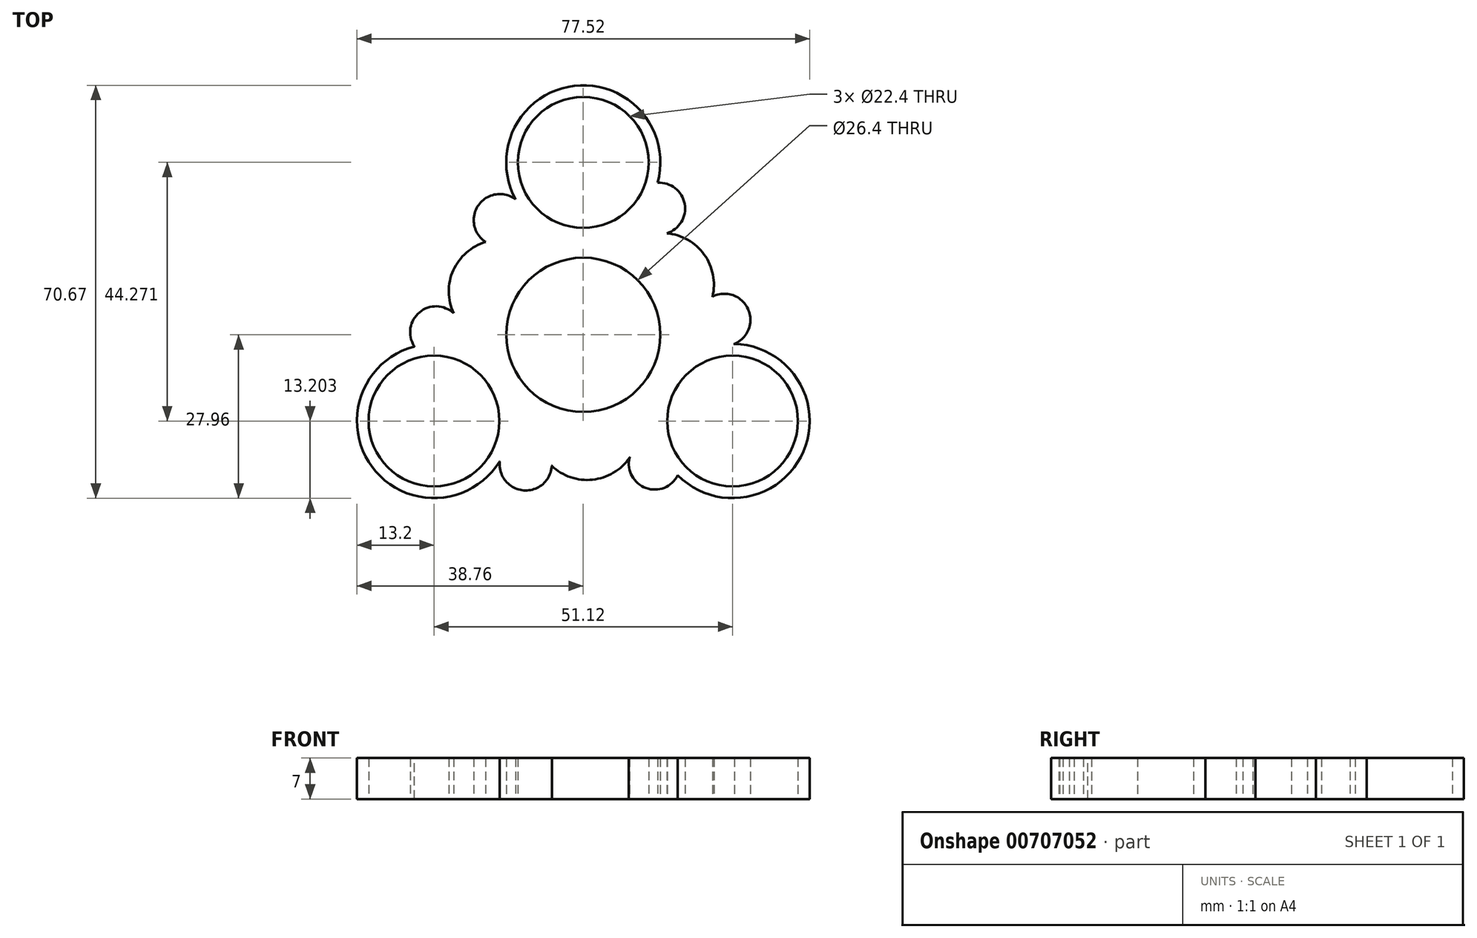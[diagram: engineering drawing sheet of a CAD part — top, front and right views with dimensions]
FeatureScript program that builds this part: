
annotation { "Feature Type Name" : "Feature", "Feature Type Description" : "" }
export const myFeature = defineFeature(function(context is Context, id is Id, definition is map)
    precondition{}
    {
        {
            var Q0;
            Q0=qCreatedBy(makeId("Top.planeOp"),FACE);
            var sketch = newSketch(context, id + "F0", { "sketchPlane" : qUnion([Q0])});
            skCircle(sketch, "E0", {"center": v(0, 0) * mm, "radius": 11.2 * mm});
            skCircle(sketch, "E1", {"center": v(0, 0) * mm, "radius": 13.2 * mm});
            skCircle(sketch, "E2", {"center": v(0, 29.51) * mm, "radius": 11.2 * mm});
            skCircle(sketch, "E3", {"center": v(0, 29.51) * mm, "radius": 13.2 * mm});
            skCircle(sketch, "E4.1.0", {"center": v(-25.56, -14.76) * mm, "radius": 11.2 * mm});
            skCircle(sketch, "E4.1.1", {"center": v(-25.56, -14.76) * mm, "radius": 13.2 * mm});
            skCircle(sketch, "E4.2.0", {"center": v(25.56, -14.76) * mm, "radius": 11.2 * mm});
            skCircle(sketch, "E4.2.1", {"center": v(25.56, -14.76) * mm, "radius": 13.2 * mm});
            skArc(sketch, "E5", {"start": v(-22.2, -2) * mm, "mid": v(-12.24, 8.63) * mm, "end": v(-11.58, 23.18) * mm});
            skArc(sketch, "E6.1.0", {"start": v(12.83, -18.23) * mm, "mid": v(-1.35, -14.91) * mm, "end": v(-14.28, -21.61) * mm});
            skArc(sketch, "E6.2.0", {"start": v(9.38, 20.22) * mm, "mid": v(13.6, 6.28) * mm, "end": v(25.86, -1.56) * mm});
            skArc(sketch, "E7", {"start": v(-10.62, 15.51) * mm, "mid": v(-21.97, 11.62) * mm, "end": v(-18.98, 0) * mm});
            skArc(sketch, "E8.1.0", {"start": v(-8.12, -16.96) * mm, "mid": v(0.93, -24.84) * mm, "end": v(9.49, -16.44) * mm});
            skArc(sketch, "E8.2.0", {"start": v(18.75, 1.45) * mm, "mid": v(21.05, 13.22) * mm, "end": v(9.49, 16.44) * mm});
            skArc(sketch, "E9", {"start": v(-11.58, 23.18) * mm, "mid": v(-17.93, 22.2) * mm, "end": v(-16.74, 15.9) * mm});
            skArc(sketch, "E10", {"start": v(-22.2, 3.69) * mm, "mid": v(-28.08, 3.83) * mm, "end": v(-28.92, -2) * mm});
            skArc(sketch, "E11.1.0", {"start": v(-14.28, -21.61) * mm, "mid": v(-10.27, -26.63) * mm, "end": v(-5.4, -22.44) * mm});
            skArc(sketch, "E11.1.1", {"start": v(7.9, -21.07) * mm, "mid": v(10.72, -26.23) * mm, "end": v(16.18, -24.05) * mm});
            skArc(sketch, "E11.2.0", {"start": v(25.86, -1.56) * mm, "mid": v(28.2, 4.43) * mm, "end": v(22.13, 6.55) * mm});
            skArc(sketch, "E11.2.1", {"start": v(14.3, 17.38) * mm, "mid": v(17.36, 22.4) * mm, "end": v(12.73, 26.04) * mm});
            skSolve(sketch);
        }
        {
            var Q0;
            Q0 = qSketchRegion(id + "F0", true);
            extrude(context, id + "F1", {"entities" : qUnion([Q0]), "depth" : 7 * mm, "offsetDistance" : 25 * mm});
        }
        {
            var Q0;
            Q0=makeQuery(id+"F1.opExtrude","SWEPT_FACE",FACE,{"disambiguationData":[OSD([sQuery(id+"F0.wireOp",EDGE,"E4.1.1")])]});
            var Q1;
            Q1=makeQuery(id+"F1.opExtrude","CAP_EDGE",EDGE,{"disambiguationData":[OSD([sQuery(id+"F0.wireOp",EDGE,"E4.2.0")])],"isStart":false});
            var Q2;
            Q2=makeQuery(id+"F1.opExtrude","CAP_EDGE",EDGE,{"disambiguationData":[OSD([sQuery(id+"F0.wireOp",EDGE,"E4.2.1")])],"isStart":false});
            var Q3;
            Q3=makeQuery(id+"F1.opExtrude","CAP_EDGE",EDGE,{"disambiguationData":[OSD([sQuery(id+"F0.wireOp",EDGE,"E4.2.1")])],"isStart":true});
            var Q4;
            Q4=makeQuery(id+"F1.opExtrude","CAP_EDGE",EDGE,{"disambiguationData":[OSD([sQuery(id+"F0.wireOp",EDGE,"E11.1.1")])],"isStart":true});
            var Q5;
            Q5=makeQuery(id+"F1.opExtrude","CAP_EDGE",EDGE,{"disambiguationData":[OSD([sQuery(id+"F0.wireOp",EDGE,"E8.1.0")])],"isStart":true});
            var Q6;
            Q6=makeQuery(id+"F1.opExtrude","CAP_EDGE",EDGE,{"disambiguationData":[OSD([sQuery(id+"F0.wireOp",EDGE,"E11.1.0")])],"isStart":true});
            var Q7;
            Q7=makeQuery(id+"F1.opExtrude","CAP_EDGE",EDGE,{"disambiguationData":[OSD([sQuery(id+"F0.wireOp",EDGE,"E8.1.0")])],"isStart":false});
            var Q8;
            Q8=makeQuery(id+"F1.opExtrude","CAP_EDGE",EDGE,{"disambiguationData":[OSD([sQuery(id+"F0.wireOp",EDGE,"E11.1.0")])],"isStart":false});
            var Q9;
            Q9=makeQuery(id+"F1.opExtrude","CAP_EDGE",EDGE,{"disambiguationData":[OSD([sQuery(id+"F0.wireOp",EDGE,"E11.1.1")])],"isStart":false});
            var Q10;
            Q10=makeQuery(id+"F1.opExtrude","CAP_EDGE",EDGE,{"disambiguationData":[OSD([sQuery(id+"F0.wireOp",EDGE,"E1")])],"isStart":false});
            var Q11;
            Q11=makeQuery(id+"F1.opExtrude","CAP_EDGE",EDGE,{"disambiguationData":[OSD([sQuery(id+"F0.wireOp",EDGE,"E11.2.0")])],"isStart":false});
            fillet(context, id + "F2", {"entities" : qUnion([Q0, Q1, Q2, Q3, Q4, Q5, Q6, Q7, Q8, Q9, Q10, Q11]), "radius" : 0.02 * mm, "tangentPropagation" : true, "allowEdgeOverflow" : false});
        }
    });
